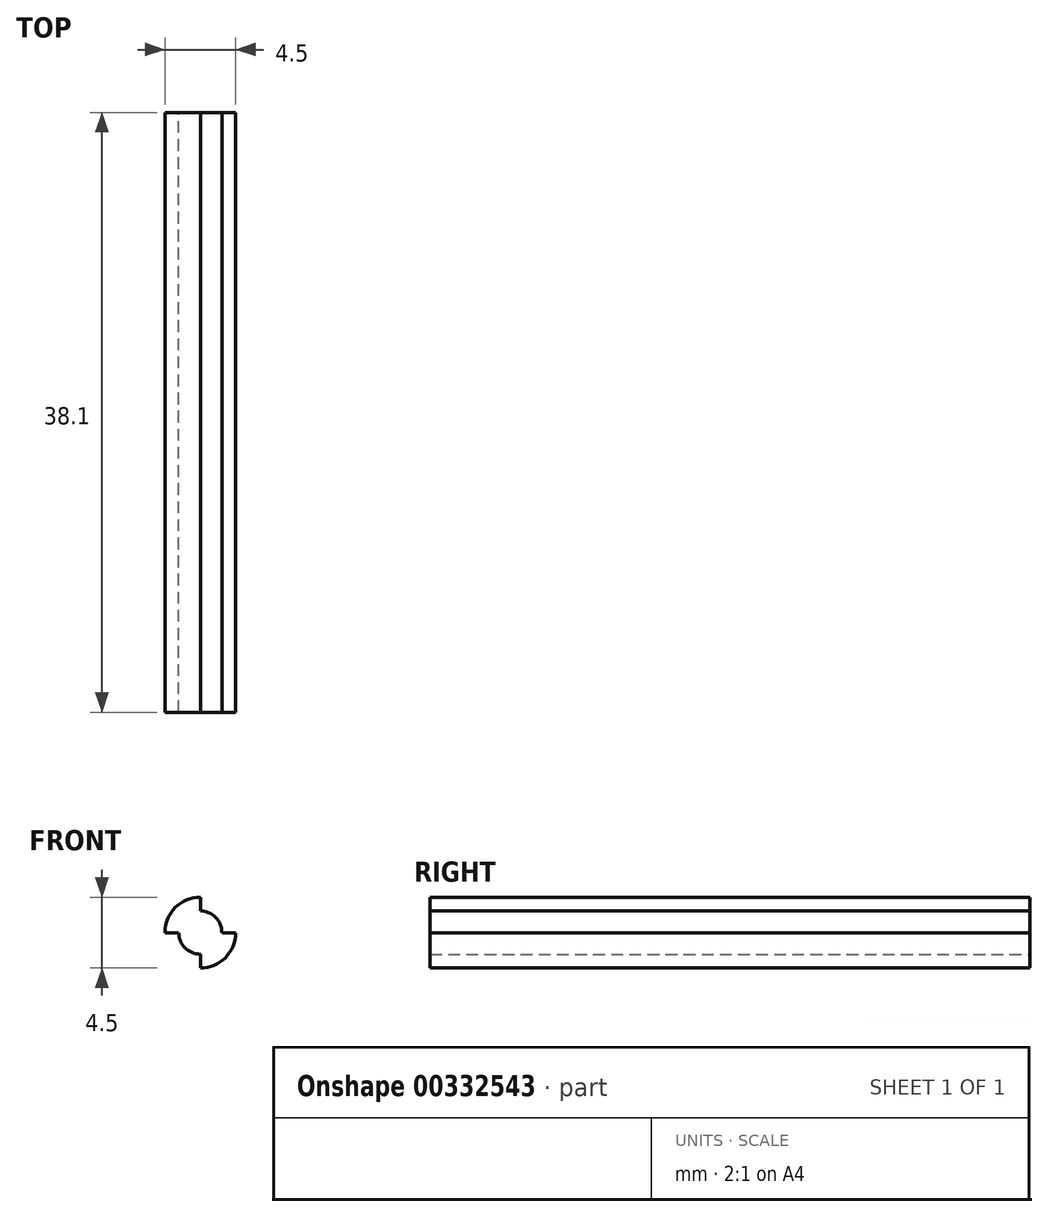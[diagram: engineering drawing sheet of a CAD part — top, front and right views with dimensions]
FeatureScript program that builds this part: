
annotation { "Feature Type Name" : "Feature", "Feature Type Description" : "" }
export const myFeature = defineFeature(function(context is Context, id is Id, definition is map)
    precondition{}
    {
        {
            var Q0;
            Q0=qCreatedBy(makeId("Front.planeOp"),FACE);
            var sketch = newSketch(context, id + "F0", { "sketchPlane" : qUnion([Q0])});
            skArc(sketch, "E0", {"start": v(0, 2.25) * mm, "mid": v(-1.59, 1.59) * mm, "end": v(-2.25, 0) * mm});
            skArc(sketch, "E1", {"start": v(-1.37, 0) * mm, "mid": v(-0.97, -0.97) * mm, "end": v(0, -1.37) * mm});
            skLineSegment(sketch, "E2", {"start": v(0, 1.37) * mm, "end": v(0, 2.25) * mm});
            skLineSegment(sketch, "E3", {"start": v(0, 2.25) * mm, "end": v(0, 1.37) * mm});
            skLineSegment(sketch, "E4", {"start": v(0, -2.25) * mm, "end": v(0, -2.25) * mm});
            skLineSegment(sketch, "E5", {"start": v(-1.37, 0) * mm, "end": v(-2.25, 0) * mm});
            skLineSegment(sketch, "E6", {"start": v(-2.25, 0) * mm, "end": v(-1.37, 0) * mm});
            skArc(sketch, "E7.trimOffspring", {"start": v(1.37, 0) * mm, "mid": v(0.97, 0.97) * mm, "end": v(0, 1.37) * mm});
            skArc(sketch, "E8.trimOffspring", {"start": v(0, -2.25) * mm, "mid": v(1.59, -1.59) * mm, "end": v(2.25, 0) * mm});
            skLineSegment(sketch, "E9.trimOffspring", {"start": v(0, -1.37) * mm, "end": v(0, -2.25) * mm});
            skLineSegment(sketch, "E10.trimOffspring", {"start": v(1.37, 0) * mm, "end": v(2.25, 0) * mm});
            skSolve(sketch);
        }
        {
            var Q0;
            Q0=makeQuery(id+"F0.imprint","IMPRINT",FACE,{"disambiguationData":[TD([[makeQuery(id+"F0.imprint","IMPRINT",EDGE,{"derivedFrom":sQuery(id+"F0.wireOp",EDGE,"E0")}),1.0]])]});
            extrude(context, id + "F1", {"entities" : qUnion([Q0]), "depth" : 38.1 * mm});
        }
    });
